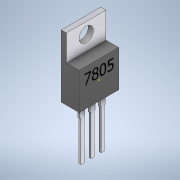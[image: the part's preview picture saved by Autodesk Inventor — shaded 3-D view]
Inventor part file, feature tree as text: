
AUTODESK INVENTOR PART (.ipt)
format: ipt  version: 2020 (Build 240168000, 168)  size: 204,288 bytes
history: native  units: mm
features: sketch x6, projected_geometry x6, extrude x5, other x1
ambient origin geometry x8: Origin, YZ Plane, XZ Plane, XY Plane, X Axis, Y Axis, Z Axis, Center Point
bodies: Body1 (feature_tree)
feature tree (18):
  other  "Sólido1"
  extrude  "Extrusión1"  Depth=9.9mm
  extrude  "Extrusión2"  Depth=2.25mm
  extrude  "Extrusión3"  Depth=1.3mm
  extrude  "Extrusión4"  Depth=6.5mm
  extrude  "Extrusión5"  Depth=3.7mm
  sketch  "Boceto6"  dims[d12=6.5mm d13=0.0mm d14=1.27mm d15=1.27mm d16=1.27mm d17=0.5mm d18=0.5mm d19=0.5mm d20=1.27mm d21=1.27mm d22=4.315mm d23=2.4mm d24=3.0mm d25=0.0mm d26=0.8mm d27=0.8mm d28=0.8mm d29=0.235mm d30=0.235mm d31=0.235mm d32=10.08mm d33=0.0mm]
  sketch  "Boceto1"  dims[d0=4.5mm d1=9.9mm]
  sketch  "Boceto2"  dims[d2=4.95mm d3=2.25mm]
  projected_geometry  "Contorno proyectado1"
  sketch  "Boceto3"  dims[d4=9.2mm d5=0.0mm d6=1.3mm]
  projected_geometry  "Contorno proyectado2"
  sketch  "Boceto4"  dims[d7=6.5mm d8=0.0mm d9=3.6mm]
  projected_geometry  "Contorno proyectado3"
  sketch  "Boceto5"  dims[d10=4.95mm d11=3.7mm]
  projected_geometry  "Contorno proyectado4"
  projected_geometry  "Contorno proyectado5"
  projected_geometry  "Contorno proyectado6"
